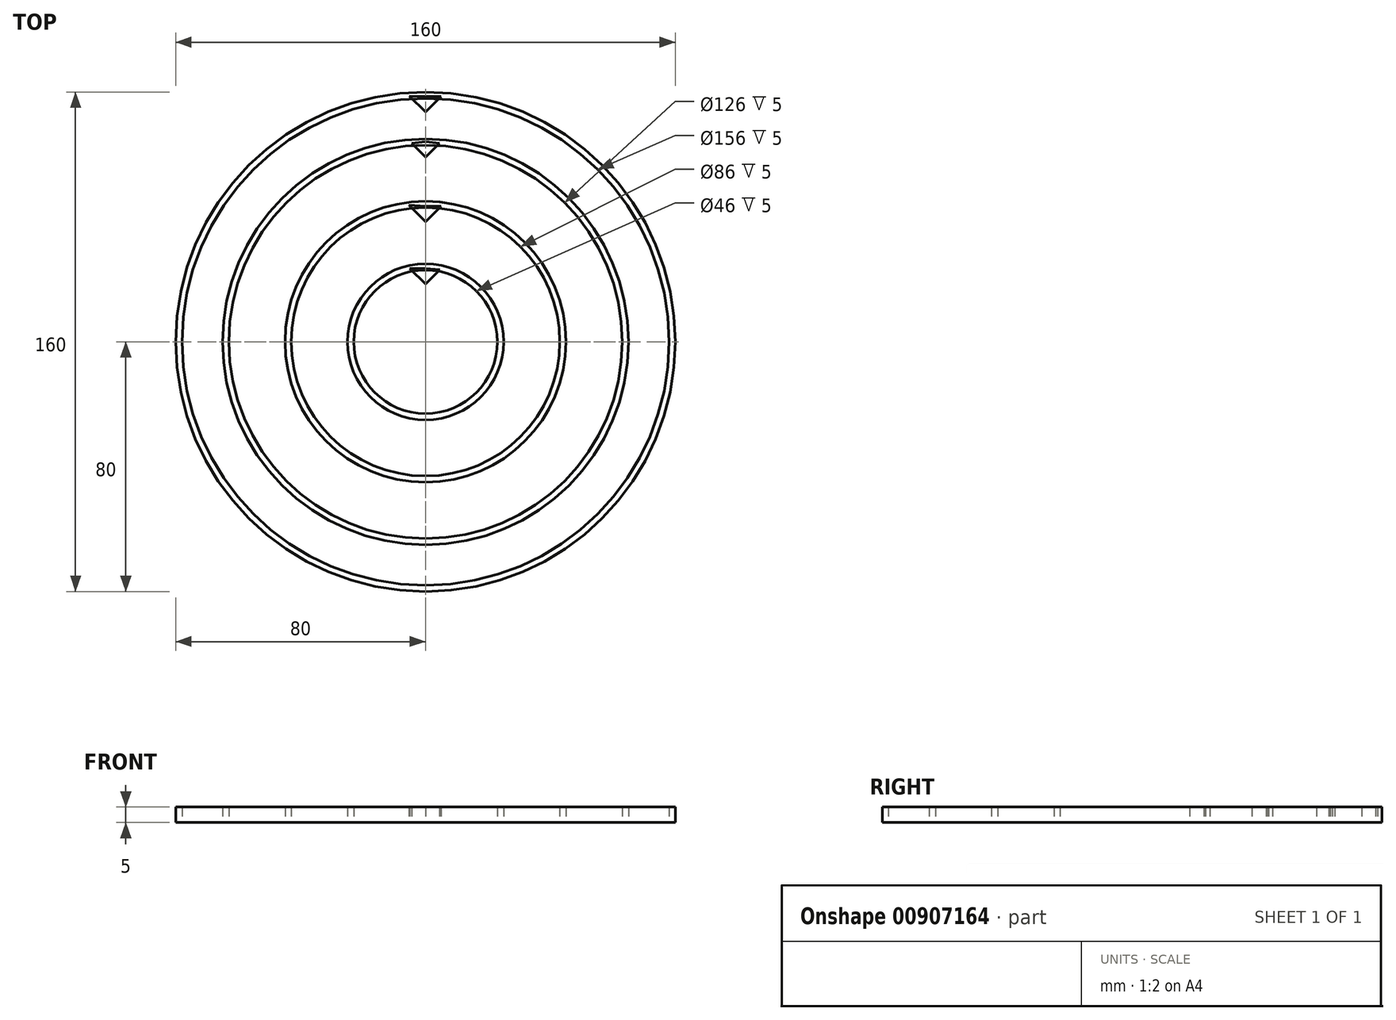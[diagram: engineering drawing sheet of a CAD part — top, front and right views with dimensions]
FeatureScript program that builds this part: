
annotation { "Feature Type Name" : "Feature", "Feature Type Description" : "" }
export const myFeature = defineFeature(function(context is Context, id is Id, definition is map)
    precondition{}
    {
        {
            var Q0;
            Q0=qCreatedBy(makeId("Top.planeOp"),FACE);
            var sketch = newSketch(context, id + "F0", { "sketchPlane" : qUnion([Q0])});
            skLineSegment(sketch, "E0.bottom", {"start": v(-80, 80) * mm, "end": v(80, 80) * mm});
            skLineSegment(sketch, "E0.top", {"start": v(-80, -80) * mm, "end": v(80, -80) * mm});
            skLineSegment(sketch, "E0.left", {"start": v(-80, 80) * mm, "end": v(-80, -80) * mm});
            skLineSegment(sketch, "E0.right", {"start": v(80, 80) * mm, "end": v(80, -80) * mm});
            skPoint(sketch, "E0.middle", {"position": v(0, 0) * mm});
            skLineSegment(sketch, "E1.bottom", {"start": v(-78, 78) * mm, "end": v(78, 78) * mm});
            skLineSegment(sketch, "E1.top", {"start": v(-78, -78) * mm, "end": v(78, -78) * mm});
            skLineSegment(sketch, "E1.left", {"start": v(-78, 78) * mm, "end": v(-78, -78) * mm});
            skLineSegment(sketch, "E1.right", {"start": v(78, 78) * mm, "end": v(78, -78) * mm});
            skLineSegment(sketch, "E2.bottom", {"start": v(-45, 45) * mm, "end": v(45, 45) * mm});
            skLineSegment(sketch, "E2.top", {"start": v(-45, -45) * mm, "end": v(45, -45) * mm});
            skLineSegment(sketch, "E2.left", {"start": v(-45, 45) * mm, "end": v(-45, -45) * mm});
            skLineSegment(sketch, "E2.right", {"start": v(45, 45) * mm, "end": v(45, -45) * mm});
            skLineSegment(sketch, "E3.bottom", {"start": v(-43, 43) * mm, "end": v(43, 43) * mm});
            skLineSegment(sketch, "E3.top", {"start": v(-43, -43) * mm, "end": v(43, -43) * mm});
            skLineSegment(sketch, "E3.left", {"start": v(-43, 43) * mm, "end": v(-43, -43) * mm});
            skLineSegment(sketch, "E3.right", {"start": v(43, 43) * mm, "end": v(43, -43) * mm});
            skLineSegment(sketch, "E4.bottom", {"start": v(-25, 25) * mm, "end": v(25, 25) * mm});
            skLineSegment(sketch, "E4.top", {"start": v(-25, -25) * mm, "end": v(25, -25) * mm});
            skLineSegment(sketch, "E4.left", {"start": v(-25, 25) * mm, "end": v(-25, -25) * mm});
            skLineSegment(sketch, "E4.right", {"start": v(25, 25) * mm, "end": v(25, -25) * mm});
            skLineSegment(sketch, "E5.bottom", {"start": v(-23, 23) * mm, "end": v(23, 23) * mm});
            skLineSegment(sketch, "E5.top", {"start": v(-23, -23) * mm, "end": v(23, -23) * mm});
            skLineSegment(sketch, "E5.left", {"start": v(-23, 23) * mm, "end": v(-23, -23) * mm});
            skLineSegment(sketch, "E5.right", {"start": v(23, 23) * mm, "end": v(23, -23) * mm});
            skLineSegment(sketch, "E6.bottom", {"start": v(-65, 65) * mm, "end": v(65, 65) * mm});
            skLineSegment(sketch, "E6.top", {"start": v(-65, -65) * mm, "end": v(65, -65) * mm});
            skLineSegment(sketch, "E6.left", {"start": v(-65, 65) * mm, "end": v(-65, -65) * mm});
            skLineSegment(sketch, "E6.right", {"start": v(65, 65) * mm, "end": v(65, -65) * mm});
            skLineSegment(sketch, "E7.bottom", {"start": v(-63, 63) * mm, "end": v(63, 63) * mm});
            skLineSegment(sketch, "E7.top", {"start": v(-63, -63) * mm, "end": v(63, -63) * mm});
            skLineSegment(sketch, "E7.left", {"start": v(-63, 63) * mm, "end": v(-63, -63) * mm});
            skLineSegment(sketch, "E7.right", {"start": v(63, 63) * mm, "end": v(63, -63) * mm});
            skSolve(sketch);
        }
        {
            var Q0;
            Q0=qCreatedBy(makeId("Top.planeOp"),FACE);
            var sketch = newSketch(context, id + "F1", { "sketchPlane" : qUnion([Q0])});
            skLineSegment(sketch, "E8", {"start": v(0, 78.6) * mm, "end": v(0, 73.6) * mm});
            skLineSegment(sketch, "E9", {"start": v(0, 73.6) * mm, "end": v(-5.12, 78.73) * mm});
            skLineSegment(sketch, "E10", {"start": v(-5.12, 78.73) * mm, "end": v(0, 78.6) * mm});
            skLineSegment(sketch, "E11", {"start": v(0, 78.6) * mm, "end": v(5, 78.6) * mm});
            skLineSegment(sketch, "E12", {"start": v(5, 78.6) * mm, "end": v(0, 73.6) * mm});
            skLineSegment(sketch, "E13", {"start": v(0, 64.13) * mm, "end": v(0, 59.13) * mm});
            skLineSegment(sketch, "E14", {"start": v(0, 59.13) * mm, "end": v(-4.45, 63.58) * mm});
            skLineSegment(sketch, "E15", {"start": v(-4.45, 63.58) * mm, "end": v(0, 64.13) * mm});
            skLineSegment(sketch, "E16", {"start": v(0, 59.13) * mm, "end": v(4.45, 63.58) * mm});
            skLineSegment(sketch, "E17", {"start": v(4.45, 63.58) * mm, "end": v(0, 64.13) * mm});
            skLineSegment(sketch, "E18", {"start": v(0, 43.45) * mm, "end": v(0, 38.45) * mm});
            skLineSegment(sketch, "E19", {"start": v(0, 38.45) * mm, "end": v(-5.32, 43.76) * mm});
            skLineSegment(sketch, "E20", {"start": v(-5.32, 43.76) * mm, "end": v(0, 43.45) * mm});
            skLineSegment(sketch, "E21", {"start": v(5, 43.45) * mm, "end": v(0, 38.45) * mm});
            skLineSegment(sketch, "E22", {"start": v(5, 43.45) * mm, "end": v(0, 43.45) * mm});
            skLineSegment(sketch, "E23", {"start": v(0, 23.5) * mm, "end": v(0, 18.5) * mm});
            skLineSegment(sketch, "E24", {"start": v(0, 18.5) * mm, "end": v(4.6, 23.1) * mm});
            skLineSegment(sketch, "E25", {"start": v(4.6, 23.1) * mm, "end": v(0, 23.5) * mm});
            skLineSegment(sketch, "E26", {"start": v(-5, 23.5) * mm, "end": v(0, 18.5) * mm});
            skLineSegment(sketch, "E27", {"start": v(-5, 23.5) * mm, "end": v(0, 23.5) * mm});
            skSolve(sketch);
        }
        {
            var Q0;
            Q0=makeQuery(id+"F1.imprint","IMPRINT",FACE,{"disambiguationData":[TD([[makeQuery(id+"F1.imprint","IMPRINT",EDGE,{"derivedFrom":sQuery(id+"F1.wireOp",EDGE,"E8")}),-1.0]])]});
            var Q1;
            Q1=makeQuery(id+"F1.imprint","IMPRINT",FACE,{"disambiguationData":[TD([[makeQuery(id+"F1.imprint","IMPRINT",EDGE,{"derivedFrom":sQuery(id+"F1.wireOp",EDGE,"E8")}),1.0]])]});
            var Q2;
            Q2=makeQuery(id+"F1.imprint","IMPRINT",FACE,{"disambiguationData":[TD([[makeQuery(id+"F1.imprint","IMPRINT",EDGE,{"derivedFrom":sQuery(id+"F1.wireOp",EDGE,"E13")}),1.0]])]});
            var Q3;
            Q3=makeQuery(id+"F1.imprint","IMPRINT",FACE,{"disambiguationData":[TD([[makeQuery(id+"F1.imprint","IMPRINT",EDGE,{"derivedFrom":sQuery(id+"F1.wireOp",EDGE,"E13")}),-1.0]])]});
            var Q4;
            Q4=makeQuery(id+"F1.imprint","IMPRINT",FACE,{"disambiguationData":[TD([[makeQuery(id+"F1.imprint","IMPRINT",EDGE,{"derivedFrom":sQuery(id+"F1.wireOp",EDGE,"E18")}),-1.0]])]});
            var Q5;
            Q5=makeQuery(id+"F1.imprint","IMPRINT",FACE,{"disambiguationData":[TD([[makeQuery(id+"F1.imprint","IMPRINT",EDGE,{"derivedFrom":sQuery(id+"F1.wireOp",EDGE,"E18")}),1.0]])]});
            var Q6;
            Q6=makeQuery(id+"F1.imprint","IMPRINT",FACE,{"disambiguationData":[TD([[makeQuery(id+"F1.imprint","IMPRINT",EDGE,{"derivedFrom":sQuery(id+"F1.wireOp",EDGE,"E23")}),-1.0]])]});
            var Q7;
            Q7=makeQuery(id+"F1.imprint","IMPRINT",FACE,{"disambiguationData":[TD([[makeQuery(id+"F1.imprint","IMPRINT",EDGE,{"derivedFrom":sQuery(id+"F1.wireOp",EDGE,"E23")}),1.0]])]});
            extrude(context, id + "F2", {"entities" : qUnion([Q0, Q1, Q2, Q3, Q4, Q5, Q6, Q7]), "depth" : 5 * mm, "offsetDistance" : 25 * mm});
        }
        {
            var Q0;
            Q0=qCreatedBy(makeId("Top.planeOp"),FACE);
            var sketch = newSketch(context, id + "F3", { "sketchPlane" : qUnion([Q0])});
            skCircle(sketch, "E28", {"center": v(0, 0) * mm, "radius": 65 * mm});
            skCircle(sketch, "E29", {"center": v(0, 0) * mm, "radius": 63 * mm});
            skCircle(sketch, "E30", {"center": v(0, 0) * mm, "radius": 80 * mm});
            skCircle(sketch, "E31", {"center": v(0, 0) * mm, "radius": 78 * mm});
            skCircle(sketch, "E32", {"center": v(0, 0) * mm, "radius": 45 * mm});
            skCircle(sketch, "E33", {"center": v(0, 0) * mm, "radius": 43 * mm});
            skCircle(sketch, "E34", {"center": v(0, 0) * mm, "radius": 25 * mm});
            skCircle(sketch, "E35", {"center": v(0, 0) * mm, "radius": 23 * mm});
            skSolve(sketch);
        }
        {
            var Q0;
            Q0=makeQuery(id+"F3.imprint","IMPRINT",FACE,{"disambiguationData":[TD([[makeQuery(id+"F3.imprint","IMPRINT",EDGE,{"derivedFrom":sQuery(id+"F3.wireOp",EDGE,"E34")}),1.0]])]});
            var Q1;
            Q1=makeQuery(id+"F3.imprint","IMPRINT",FACE,{"disambiguationData":[TD([[makeQuery(id+"F3.imprint","IMPRINT",EDGE,{"derivedFrom":sQuery(id+"F3.wireOp",EDGE,"E32")}),1.0]])]});
            var Q2;
            Q2=makeQuery(id+"F3.imprint","IMPRINT",FACE,{"disambiguationData":[TD([[makeQuery(id+"F3.imprint","IMPRINT",EDGE,{"derivedFrom":sQuery(id+"F3.wireOp",EDGE,"E30")}),1.0]])]});
            var Q3;
            Q3=makeQuery(id+"F3.imprint","IMPRINT",FACE,{"disambiguationData":[TD([[makeQuery(id+"F3.imprint","IMPRINT",EDGE,{"derivedFrom":sQuery(id+"F3.wireOp",EDGE,"E28")}),1.0]])]});
            extrude(context, id + "F4", {"entities" : qUnion([Q0, Q1, Q2, Q3]), "depth" : 5 * mm, "offsetDistance" : 25 * mm});
        }
    });
